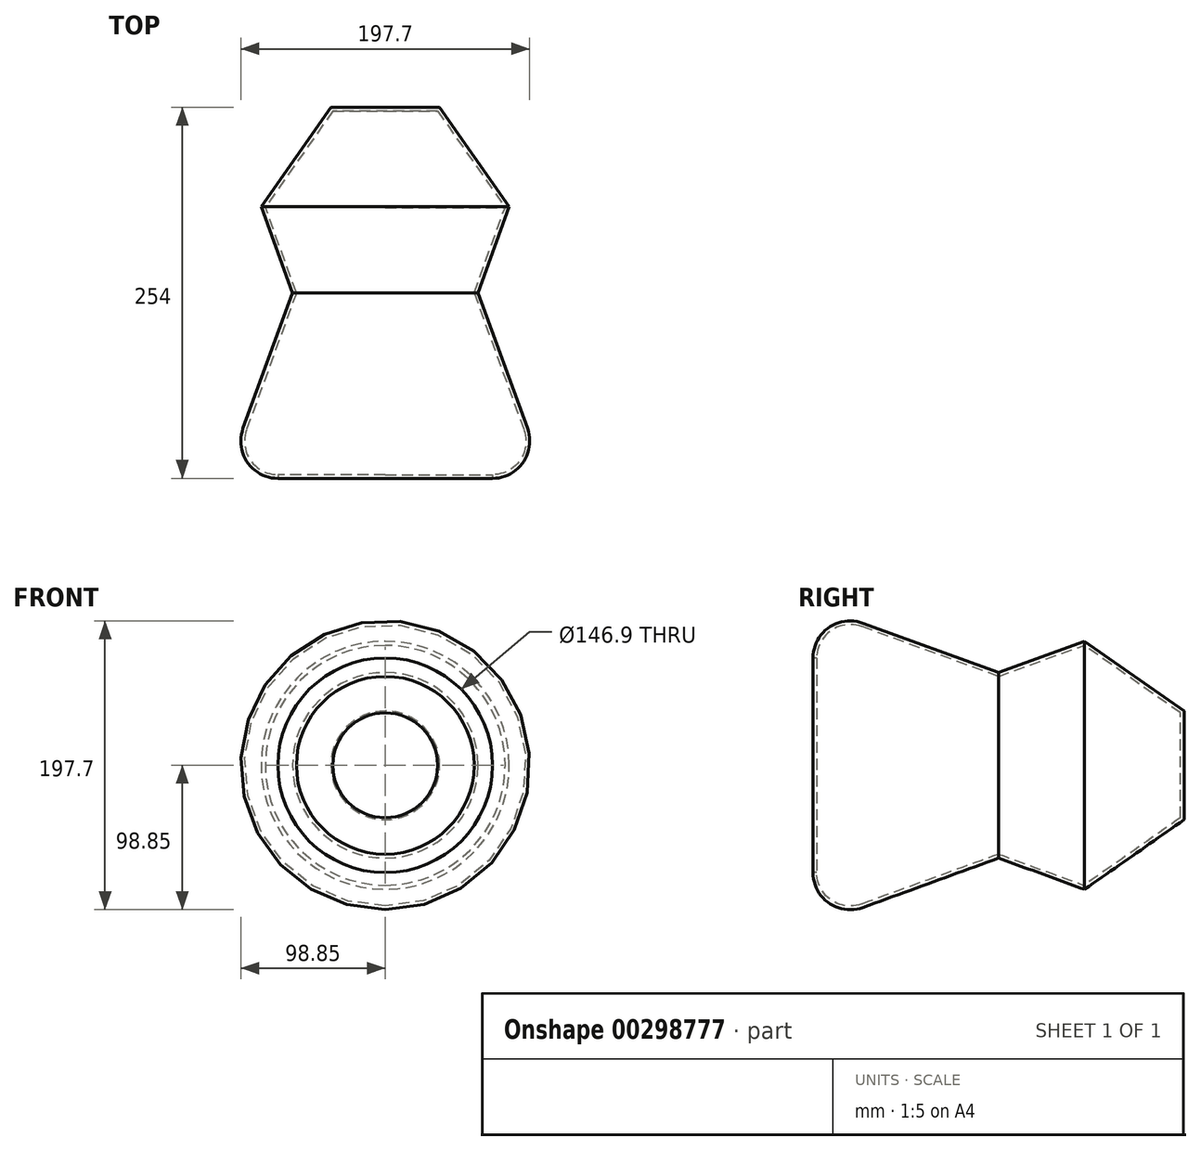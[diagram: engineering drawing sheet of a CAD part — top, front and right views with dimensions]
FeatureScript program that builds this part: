
annotation { "Feature Type Name" : "Feature", "Feature Type Description" : "" }
export const myFeature = defineFeature(function(context is Context, id is Id, definition is map)
    precondition{}
    {
        {
            var Q0;
            Q0=qCreatedBy(makeId("Front.planeOp"),FACE);
            var sketch = newSketch(context, id + "F0", { "sketchPlane" : qUnion([Q0])});
            skCircle(sketch, "E0", {"center": v(0, 0) * mm, "radius": 63.5 * mm});
            skSolve(sketch);
        }
        {
            var Q0;
            Q0=makeQuery(id+"F0.imprint","IMPRINT",FACE,{"disambiguationData":[TD([[makeQuery(id+"F0.imprint","IMPRINT",EDGE,{"derivedFrom":sQuery(id+"F0.wireOp",EDGE,"E0")}),1.0]])]});
            extrude(context, id + "F1", {"entities" : qUnion([Q0]), "endBound" : BoundingType.SYMMETRIC, "depth" : 254 * mm, "hasDraft" : true, "draftAngle" : 20 * degree});
        }
        {
            var Q0;
            Q0=makeQuery(id+"F1.opExtrude","CAP_FACE",FACE,{"disambiguationData":[OSD([sQuery(id+"F0.wireOp",EDGE,"E0")])],"isStart":true});
            chamfer(context, id + "F2", {"entities" : qUnion([Q0]), "width" : 50.8 * mm, "tangentPropagation" : true});
        }
        {
            var Q0;
            Q0=makeQuery(id+"F1.opExtrude","CAP_EDGE",EDGE,{"disambiguationData":[OSD([sQuery(id+"F0.wireOp",EDGE,"E0")])],"isStart":false});
            fillet(context, id + "F3", {"entities" : qUnion([Q0]), "radius" : 25.4 * mm, "tangentPropagation" : true, "allowEdgeOverflow" : false});
        }
        {
            var Q0;
            Q0=makeQuery(id+"F1.opExtrude","CAP_FACE",FACE,{"disambiguationData":[OSD([sQuery(id+"F0.wireOp",EDGE,"E0")])],"isStart":false});
            shell(context, id + "F4", {"entities" : qUnion([Q0]), "thickness" : 2.54 * mm});
        }
    });
